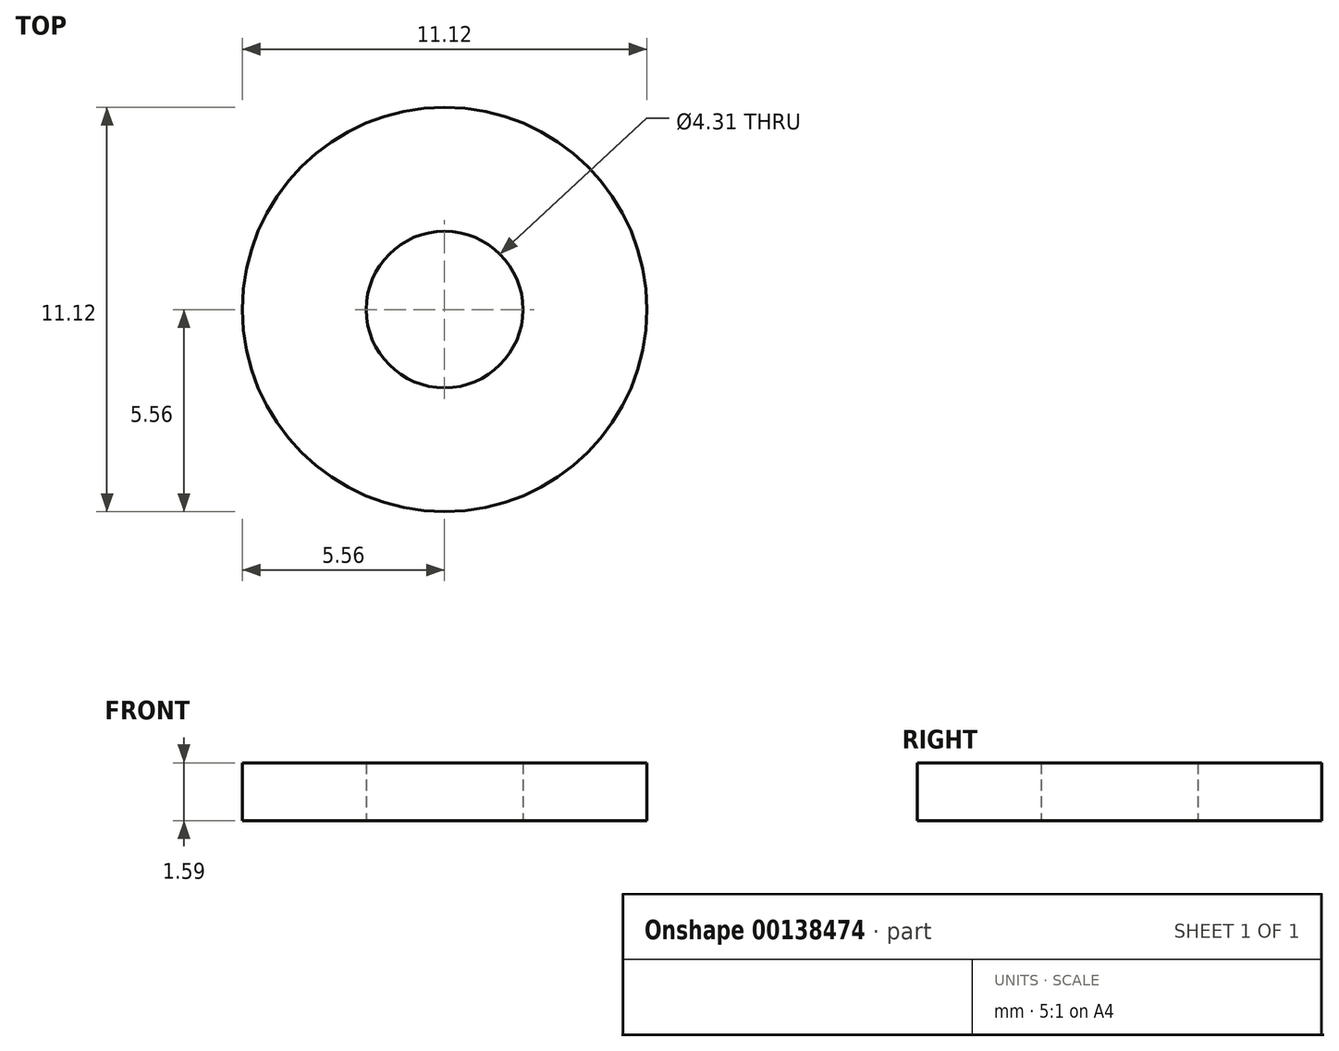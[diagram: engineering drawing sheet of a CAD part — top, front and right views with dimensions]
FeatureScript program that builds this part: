
annotation { "Feature Type Name" : "Feature", "Feature Type Description" : "" }
export const myFeature = defineFeature(function(context is Context, id is Id, definition is map)
    precondition{}
    {
        {
            var Q0;
            Q0=qCreatedBy(makeId("Top.planeOp"),FACE);
            var sketch = newSketch(context, id + "F0", { "sketchPlane" : qUnion([Q0])});
            skCircle(sketch, "E0", {"center": v(0, 0) * mm, "radius": 5.56 * mm});
            skCircle(sketch, "E1", {"center": v(0, 0) * mm, "radius": 2.15 * mm});
            skSolve(sketch);
        }
        {
            var Q0;
            Q0=qSketchRegion(id+"F0",true);
            extrude(context, id + "F1", {"entities" : qUnion([Q0]), "depth" : 1.59 * mm});
        }
    });
